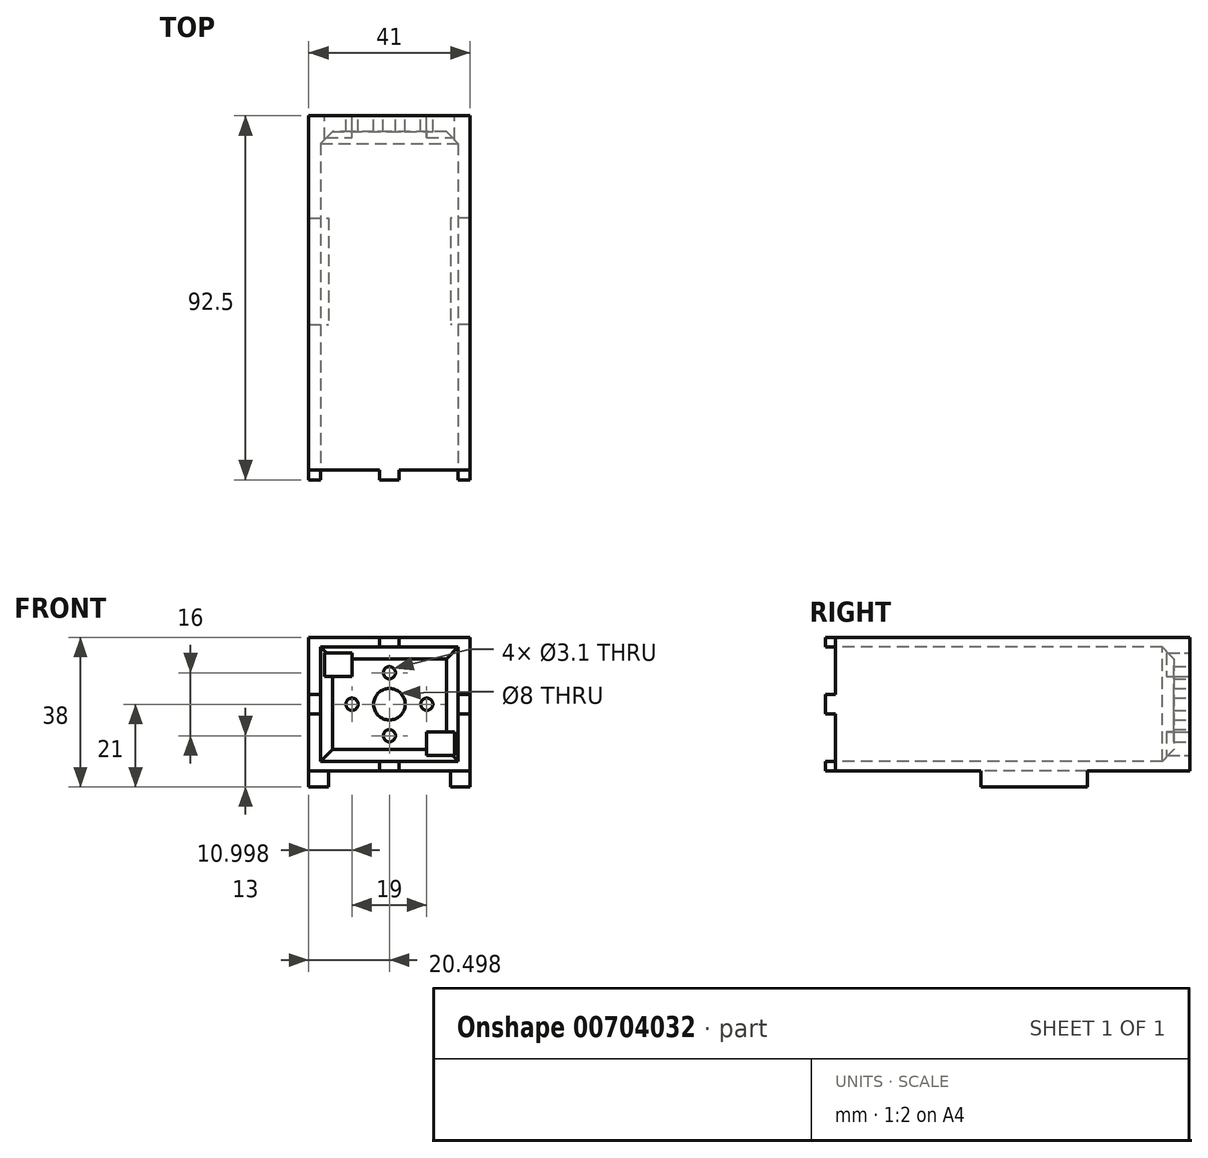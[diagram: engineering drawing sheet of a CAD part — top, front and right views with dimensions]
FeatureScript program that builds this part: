
annotation { "Feature Type Name" : "Feature", "Feature Type Description" : "" }
export const myFeature = defineFeature(function(context is Context, id is Id, definition is map)
    precondition{}
    {
        {
            var Q0;
            Q0=qCreatedBy(makeId("Top.planeOp"),FACE);
            var sketch = newSketch(context, id + "F0", { "sketchPlane" : qUnion([Q0])});
            skLineSegment(sketch, "E0.bottom", {"start": v(-22.2, 49.2) * mm, "end": v(18.8, 49.2) * mm});
            skLineSegment(sketch, "E0.top", {"start": v(-22.2, -40.8) * mm, "end": v(18.8, -40.8) * mm});
            skLineSegment(sketch, "E0.left", {"start": v(-22.2, 49.2) * mm, "end": v(-22.2, -40.8) * mm});
            skLineSegment(sketch, "E0.right", {"start": v(18.8, 49.2) * mm, "end": v(18.8, -40.8) * mm});
            skSolve(sketch);
        }
        {
            var Q0;
            Q0=makeQuery(id+"F0.imprint","IMPRINT",FACE,{"disambiguationData":[TD([[makeQuery(id+"F0.imprint","IMPRINT",EDGE,{"derivedFrom":sQuery(id+"F0.wireOp",EDGE,"E0.bottom")}),-1.0]])]});
            extrude(context, id + "F1", {"entities" : qUnion([Q0]), "depth" : 34 * mm, "offsetDistance" : 25 * mm});
        }
        {
            var Q0;
            Q0=makeQuery(id+"F1.opExtrude","SWEPT_FACE",FACE,{"disambiguationData":[OSD([sQuery(id+"F0.wireOp",EDGE,"E0.top")])]});
            var sketch = newSketch(context, id + "F2", { "sketchPlane" : qUnion([Q0])});
            skLineSegment(sketch, "E1.bottom", {"start": v(-19.2, 31.5) * mm, "end": v(15.8, 31.5) * mm});
            skLineSegment(sketch, "E1.top", {"start": v(-19.2, 2.5) * mm, "end": v(15.8, 2.5) * mm});
            skLineSegment(sketch, "E1.left", {"start": v(-19.2, 31.5) * mm, "end": v(-19.2, 2.5) * mm});
            skLineSegment(sketch, "E1.right", {"start": v(15.8, 31.5) * mm, "end": v(15.8, 2.5) * mm});
            skSolve(sketch);
        }
        {
            var Q0;
            Q0=makeQuery(id+"F2.imprint","IMPRINT",FACE,{"disambiguationData":[TD([[makeQuery(id+"F2.imprint","IMPRINT",EDGE,{"derivedFrom":sQuery(id+"F2.wireOp",EDGE,"E1.bottom")}),-1.0]])]});
            extrude(context, id + "F3", {"entities" : qUnion([Q0]), "operationType" : NewBodyOperationType.REMOVE, "oppositeDirection" : true, "depth" : 86 * mm, "offsetDistance" : 25 * mm});
        }
        {
            var Q0;
            Q0=makeQuery(id+"F1.opExtrude","SWEPT_FACE",FACE,{"disambiguationData":[OSD([sQuery(id+"F0.wireOp",EDGE,"E0.bottom")])]});
            var sketch = newSketch(context, id + "F4", { "sketchPlane" : qUnion([Q0])});
            skCircle(sketch, "E2", {"center": v(1.7, 17) * mm, "radius": 4 * mm});
            skCircle(sketch, "E3", {"center": v(-7.8, 17) * mm, "radius": 1.55 * mm});
            skCircle(sketch, "E4", {"center": v(11.2, 17) * mm, "radius": 1.55 * mm});
            skLineSegment(sketch, "E5.bottom", {"start": v(11.2, 30) * mm, "end": v(18.2, 30) * mm});
            skLineSegment(sketch, "E5.top", {"start": v(11.2, 24) * mm, "end": v(18.2, 24) * mm});
            skLineSegment(sketch, "E5.left", {"start": v(11.2, 30) * mm, "end": v(11.2, 24) * mm});
            skLineSegment(sketch, "E5.right", {"start": v(18.2, 30) * mm, "end": v(18.2, 24) * mm});
            skLineSegment(sketch, "E6.bottom", {"start": v(-14.8, 10) * mm, "end": v(-7.8, 10) * mm});
            skLineSegment(sketch, "E6.top", {"start": v(-14.8, 4) * mm, "end": v(-7.8, 4) * mm});
            skLineSegment(sketch, "E6.left", {"start": v(-14.8, 10) * mm, "end": v(-14.8, 4) * mm});
            skLineSegment(sketch, "E6.right", {"start": v(-7.8, 10) * mm, "end": v(-7.8, 4) * mm});
            skCircle(sketch, "E7", {"center": v(1.7, 9) * mm, "radius": 1.55 * mm});
            skCircle(sketch, "E8", {"center": v(1.7, 25) * mm, "radius": 1.55 * mm});
            skSolve(sketch);
        }
        {
            var Q0;
            Q0=makeQuery(id+"F4.imprint","IMPRINT",FACE,{"disambiguationData":[TD([[makeQuery(id+"F4.imprint","IMPRINT",EDGE,{"derivedFrom":sQuery(id+"F4.wireOp",EDGE,"E6.bottom")}),-1.0]])]});
            var Q1;
            Q1=makeQuery(id+"F4.imprint","IMPRINT",FACE,{"disambiguationData":[TD([[makeQuery(id+"F4.imprint","IMPRINT",EDGE,{"derivedFrom":sQuery(id+"F4.wireOp",EDGE,"E3")}),1.0]])]});
            var Q2;
            Q2=makeQuery(id+"F4.imprint","IMPRINT",FACE,{"disambiguationData":[TD([[makeQuery(id+"F4.imprint","IMPRINT",EDGE,{"derivedFrom":sQuery(id+"F4.wireOp",EDGE,"E8")}),1.0]])]});
            var Q3;
            Q3=makeQuery(id+"F4.imprint","IMPRINT",FACE,{"disambiguationData":[TD([[makeQuery(id+"F4.imprint","IMPRINT",EDGE,{"derivedFrom":sQuery(id+"F4.wireOp",EDGE,"E2")}),1.0]])]});
            var Q4;
            Q4=makeQuery(id+"F4.imprint","IMPRINT",FACE,{"disambiguationData":[TD([[makeQuery(id+"F4.imprint","IMPRINT",EDGE,{"derivedFrom":sQuery(id+"F4.wireOp",EDGE,"E7")}),1.0]])]});
            var Q5;
            Q5=makeQuery(id+"F4.imprint","IMPRINT",FACE,{"disambiguationData":[TD([[makeQuery(id+"F4.imprint","IMPRINT",EDGE,{"derivedFrom":sQuery(id+"F4.wireOp",EDGE,"E4")}),1.0]])]});
            var Q6;
            Q6=makeQuery(id+"F4.imprint","IMPRINT",FACE,{"disambiguationData":[TD([[makeQuery(id+"F4.imprint","IMPRINT",EDGE,{"derivedFrom":sQuery(id+"F4.wireOp",EDGE,"E5.bottom")}),-1.0]])]});
            extrude(context, id + "F5", {"entities" : qUnion([Q0, Q1, Q2, Q3, Q4, Q5, Q6]), "operationType" : NewBodyOperationType.REMOVE, "endBound" : BoundingType.UP_TO_NEXT, "oppositeDirection" : true, "depth" : 25 * mm, "offsetDistance" : 25 * mm});
        }
        {
            var Q0;
            Q0=makeQuery(id+"F1.opExtrude","SWEPT_FACE",FACE,{"disambiguationData":[OSD([sQuery(id+"F0.wireOp",EDGE,"E0.top")])]});
            var sketch = newSketch(context, id + "F6", { "sketchPlane" : qUnion([Q0])});
            skLineSegment(sketch, "E9.bottom", {"start": v(-4.2, 34) * mm, "end": v(0.8, 34) * mm});
            skLineSegment(sketch, "E9.top", {"start": v(-4.2, 31.5) * mm, "end": v(0.8, 31.5) * mm});
            skLineSegment(sketch, "E9.left", {"start": v(-4.2, 34) * mm, "end": v(-4.2, 31.5) * mm});
            skLineSegment(sketch, "E9.right", {"start": v(0.8, 34) * mm, "end": v(0.8, 31.5) * mm});
            skLineSegment(sketch, "E10.bottom", {"start": v(-4.2, 2.5) * mm, "end": v(0.8, 2.5) * mm});
            skLineSegment(sketch, "E10.top", {"start": v(-4.2, 0) * mm, "end": v(0.8, 0) * mm});
            skLineSegment(sketch, "E10.left", {"start": v(-4.2, 2.5) * mm, "end": v(-4.2, 0) * mm});
            skLineSegment(sketch, "E10.right", {"start": v(0.8, 2.5) * mm, "end": v(0.8, 0) * mm});
            skLineSegment(sketch, "E11.bottom", {"start": v(-22.2, 19.5) * mm, "end": v(-19.2, 19.5) * mm});
            skLineSegment(sketch, "E11.top", {"start": v(-22.2, 14.5) * mm, "end": v(-19.2, 14.5) * mm});
            skLineSegment(sketch, "E11.left", {"start": v(-22.2, 19.5) * mm, "end": v(-22.2, 14.5) * mm});
            skLineSegment(sketch, "E11.right", {"start": v(-19.2, 19.5) * mm, "end": v(-19.2, 14.5) * mm});
            skLineSegment(sketch, "E12.bottom", {"start": v(15.8, 19.5) * mm, "end": v(18.8, 19.5) * mm});
            skLineSegment(sketch, "E12.top", {"start": v(15.8, 14.5) * mm, "end": v(18.8, 14.5) * mm});
            skLineSegment(sketch, "E12.left", {"start": v(15.8, 19.5) * mm, "end": v(15.8, 14.5) * mm});
            skLineSegment(sketch, "E12.right", {"start": v(18.8, 19.5) * mm, "end": v(18.8, 14.5) * mm});
            skSolve(sketch);
        }
        {
            var Q0;
            Q0=makeQuery(id+"F6.imprint","IMPRINT",FACE,{"disambiguationData":[TD([[makeQuery(id+"F6.imprint","IMPRINT",EDGE,{"derivedFrom":sQuery(id+"F6.wireOp",EDGE,"E9.bottom")}),-1.0]])]});
            var Q1;
            Q1=makeQuery(id+"F6.imprint","IMPRINT",FACE,{"disambiguationData":[TD([[makeQuery(id+"F6.imprint","IMPRINT",EDGE,{"derivedFrom":sQuery(id+"F6.wireOp",EDGE,"E11.bottom")}),-1.0]])]});
            var Q2;
            Q2=makeQuery(id+"F6.imprint","IMPRINT",FACE,{"disambiguationData":[TD([[makeQuery(id+"F6.imprint","IMPRINT",EDGE,{"derivedFrom":sQuery(id+"F6.wireOp",EDGE,"E12.bottom")}),-1.0]])]});
            var Q3;
            Q3=makeQuery(id+"F6.imprint","IMPRINT",FACE,{"disambiguationData":[TD([[makeQuery(id+"F6.imprint","IMPRINT",EDGE,{"derivedFrom":sQuery(id+"F6.wireOp",EDGE,"E10.bottom")}),-1.0]])]});
            extrude(context, id + "F7", {"entities" : qUnion([Q0, Q1, Q2, Q3]), "operationType" : NewBodyOperationType.ADD, "depth" : 2.5 * mm, "offsetDistance" : 25 * mm});
        }
        {
            var Q0;
            Q0=makeQuery(id+"F7.boolean.opBoolean","MERGE",FACE,{"derivedFrom":[makeQuery(id+"F1.opExtrude","CAP_FACE",FACE,{"disambiguationData":[OSD([sQuery(id+"F0.wireOp",EDGE,"E0.bottom"),sQuery(id+"F0.wireOp",EDGE,"E0.top"),sQuery(id+"F0.wireOp",EDGE,"E0.left"),sQuery(id+"F0.wireOp",EDGE,"E0.right")])],"isStart":true}),makeQuery(id+"F7.opExtrude","SWEPT_FACE",FACE,{"disambiguationData":[OSD([sQuery(id+"F6.wireOp",EDGE,"E10.top")])]})]});
            var sketch = newSketch(context, id + "F8", { "sketchPlane" : qUnion([Q0])});
            skLineSegment(sketch, "E13.bottom", {"start": v(18.8, -23.2) * mm, "end": v(13.8, -23.2) * mm});
            skLineSegment(sketch, "E13.top", {"start": v(18.8, 3.8) * mm, "end": v(13.8, 3.8) * mm});
            skLineSegment(sketch, "E13.left", {"start": v(18.8, -23.2) * mm, "end": v(18.8, 3.8) * mm});
            skLineSegment(sketch, "E13.right", {"start": v(13.8, -23.2) * mm, "end": v(13.8, 3.8) * mm});
            skLineSegment(sketch, "E14.bottom", {"start": v(-22.2, -23.2) * mm, "end": v(-17.2, -23.2) * mm});
            skLineSegment(sketch, "E14.top", {"start": v(-22.2, 3.8) * mm, "end": v(-17.2, 3.8) * mm});
            skLineSegment(sketch, "E14.left", {"start": v(-22.2, -23.2) * mm, "end": v(-22.2, 3.8) * mm});
            skLineSegment(sketch, "E14.right", {"start": v(-17.2, -23.2) * mm, "end": v(-17.2, 3.8) * mm});
            skSolve(sketch);
        }
        {
            var Q0;
            Q0=makeQuery(id+"F8.imprint","IMPRINT",FACE,{"disambiguationData":[TD([[makeQuery(id+"F8.imprint","IMPRINT",EDGE,{"derivedFrom":sQuery(id+"F8.wireOp",EDGE,"E14.bottom")}),1.0]])]});
            var Q1;
            Q1=makeQuery(id+"F8.imprint","IMPRINT",FACE,{"disambiguationData":[TD([[makeQuery(id+"F8.imprint","IMPRINT",EDGE,{"derivedFrom":sQuery(id+"F8.wireOp",EDGE,"E13.bottom")}),-1.0]])]});
            extrude(context, id + "F9", {"entities" : qUnion([Q0, Q1]), "operationType" : NewBodyOperationType.ADD, "depth" : 4 * mm, "offsetDistance" : 25 * mm});
        }
        {
            var Q0;
            Q0=makeQuery(id+"F3.boolean.opBoolean","COPY",EDGE,{"derivedFrom":makeQuery(id+"F3.opExtrude","CAP_EDGE",EDGE,{"disambiguationData":[OSD([sQuery(id+"F2.wireOp",EDGE,"E1.left")])],"isStart":false})});
            var Q1;
            Q1=makeQuery(id+"F3.boolean.opBoolean","COPY",EDGE,{"derivedFrom":makeQuery(id+"F3.opExtrude","CAP_EDGE",EDGE,{"disambiguationData":[OSD([sQuery(id+"F2.wireOp",EDGE,"E1.right")])],"isStart":false})});
            var Q2;
            Q2=makeQuery(id+"F3.boolean.opBoolean","COPY",EDGE,{"derivedFrom":makeQuery(id+"F3.opExtrude","CAP_EDGE",EDGE,{"disambiguationData":[OSD([sQuery(id+"F2.wireOp",EDGE,"E1.bottom")])],"isStart":false})});
            var Q3;
            Q3=makeQuery(id+"F3.boolean.opBoolean","COPY",EDGE,{"derivedFrom":makeQuery(id+"F3.opExtrude","CAP_EDGE",EDGE,{"disambiguationData":[OSD([sQuery(id+"F2.wireOp",EDGE,"E1.top")])],"isStart":false})});
            chamfer(context, id + "F10", {"entities" : qUnion([Q0, Q1, Q2, Q3]), "width" : 3 * mm, "tangentPropagation" : true});
        }
    });
